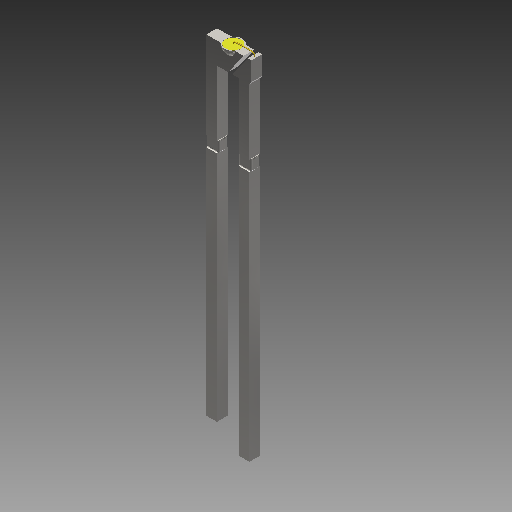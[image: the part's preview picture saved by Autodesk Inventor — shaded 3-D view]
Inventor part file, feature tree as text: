
AUTODESK INVENTOR PART (.ipt)
format: ipt  version: 2019.4 (Build 234330000, 330)  size: 322,560 bytes
history: native  units: mm
features: sketch x7, fillet x4, revolve x3, other x2, extrude x2, projected_geometry x2, sweep x1
ambient origin geometry x8: Origin, YZ Plane, XZ Plane, XY Plane, X Axis, Y Axis, Z Axis, Center Point
bodies: Body1 (feature_tree), Body2 (feature_tree)
feature tree (21):
  other  "Sólido1"
  extrude  "Extrusión1"  Depth=0.98mm
  extrude  "Extrusión2"  Depth=0.98mm
  fillet  "Empalme6"  Radius=4.0mm
  fillet  "Empalme7"  Radius=2.0mm
  fillet  "Empalme8"  Radius=1.0mm
  fillet  "Empalme9"  Radius=4.0mm
  revolve  "Revolución1"  [1 undecoded]
  revolve  "Revolución2"  [1 undecoded]
  revolve  "Revolución3"  [1 undecoded]
  sweep  "Barrido1"
  sketch  "Boceto1"  dims[d0=0.98mm d1=0.98mm]
  sketch  "Boceto2"  dims[d2=4.0mm d3=0.98mm d4=4.0mm d5=2.0mm d6=1.0mm d7=4.0mm]
  sketch  "Boceto3"  dims[d8=2.0mm d9=21.816616mm]
  sketch  "Boceto4"  dims[d10=9.599311mm d11=1.0mm]
  sketch  "Boceto5"  dims[d12=28.1mm d13=1.7mm]
  other  "Sólido2"
  sketch  "Boceto6"  dims[d14=0.98mm d15=0.0mm d16=1.18mm]
  projected_geometry  "Contorno proyectado1"
  projected_geometry  "Contorno proyectado2"
  sketch  "Boceto7"  dims[d17=1.18mm d20=0.1mm d21=0.1mm d22=0.78mm d23=0.0mm d29=0.1mm d30=0.1mm d31=0.1mm d32=0.1mm d33=180.0deg d34=180.0deg d35=180.0deg d36=0.1mm d37=0.0mm d38=0.0mm]
note: 3 required parameter values undecoded (feature->parameter linkage not recoverable at this tier; creation-order binding heuristic only, values carry confidence <= 0.55)
